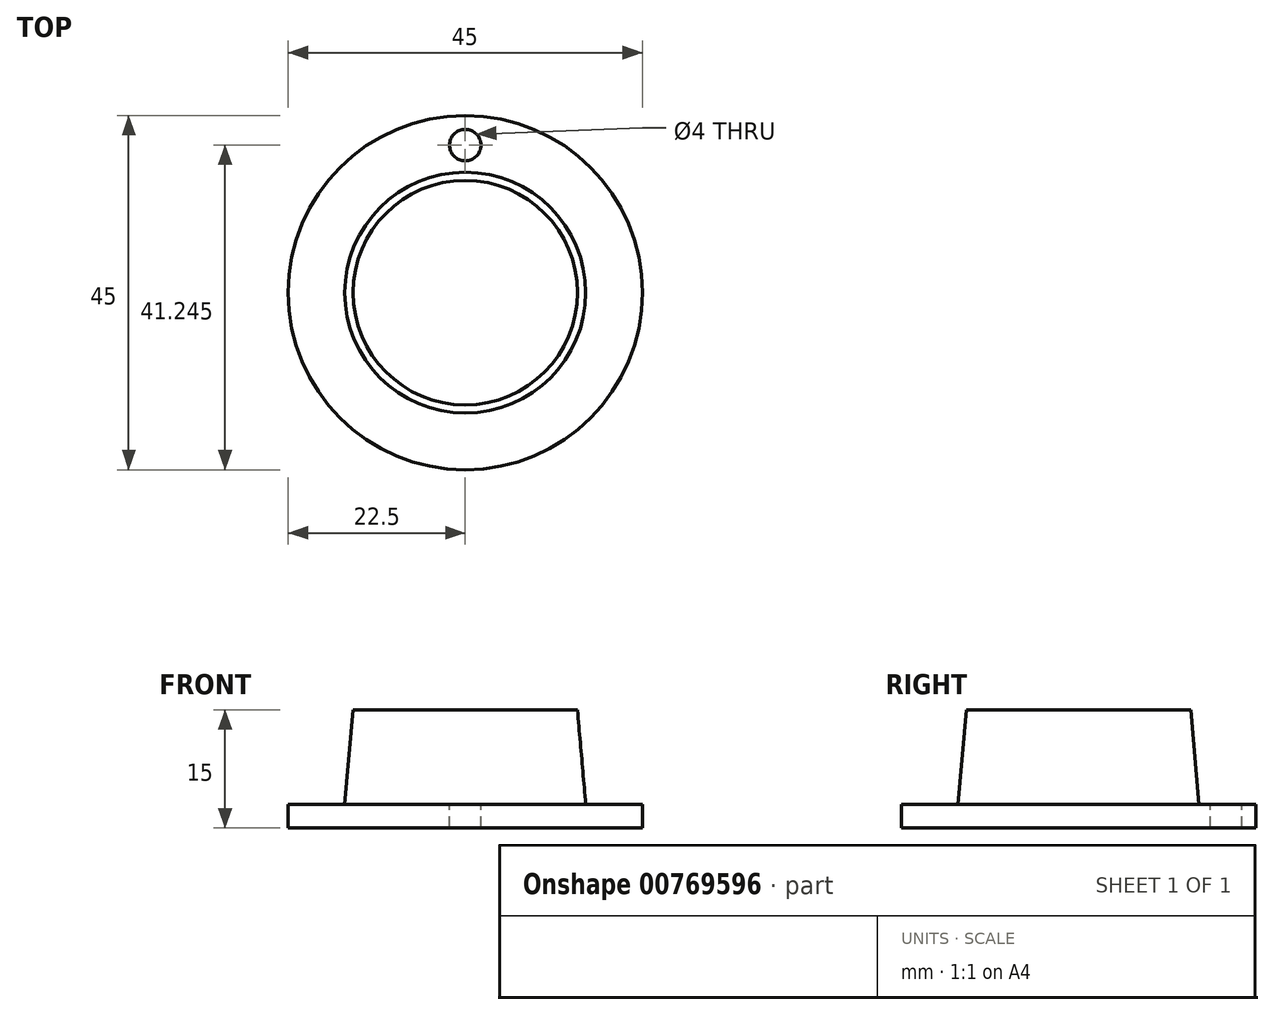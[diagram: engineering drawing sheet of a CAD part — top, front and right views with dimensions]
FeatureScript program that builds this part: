
annotation { "Feature Type Name" : "Feature", "Feature Type Description" : "" }
export const myFeature = defineFeature(function(context is Context, id is Id, definition is map)
    precondition{}
    {
        {
            var Q0;
            Q0=qCreatedBy(makeId("Top.planeOp"),FACE);
            var sketch = newSketch(context, id + "F0", { "sketchPlane" : qUnion([Q0])});
            skCircle(sketch, "E0", {"center": v(0, 0) * mm, "radius": 22.5 * mm});
            skCircle(sketch, "E1", {"center": v(0, 0) * mm, "radius": 15.3 * mm});
            skSolve(sketch);
        }
        {
            var Q0;
            Q0=makeQuery(id+"F0.imprint","IMPRINT",FACE,{"disambiguationData":[TD([[makeQuery(id+"F0.imprint","IMPRINT",EDGE,{"derivedFrom":sQuery(id+"F0.wireOp",EDGE,"E0")}),1.0]])]});
            var Q1;
            Q1=makeQuery(id+"F0.imprint","IMPRINT",FACE,{"disambiguationData":[TD([[makeQuery(id+"F0.imprint","IMPRINT",EDGE,{"derivedFrom":sQuery(id+"F0.wireOp",EDGE,"E1")}),1.0]])]});
            extrude(context, id + "F1", {"entities" : qUnion([Q0, Q1]), "depth" : 3 * mm, "offsetDistance" : 25 * mm});
        }
        {
            var Q0;
            Q0=makeQuery(id+"F1.opExtrude","CAP_FACE",FACE,{"disambiguationData":[OSD([sQuery(id+"F0.wireOp",EDGE,"E0")])],"isStart":false});
            var sketch = newSketch(context, id + "F2", { "sketchPlane" : qUnion([Q0])});
            skCircle(sketch, "E2", {"center": v(0, 0) * mm, "radius": 15.3 * mm});
            skSolve(sketch);
        }
        {
            var Q0;
            Q0=makeQuery(id+"F2.imprint","IMPRINT",FACE,{"disambiguationData":[TD([[makeQuery(id+"F2.imprint","IMPRINT",EDGE,{"derivedFrom":sQuery(id+"F2.wireOp",EDGE,"E2")}),1.0]])]});
            extrude(context, id + "F3", {"entities" : qUnion([Q0]), "operationType" : NewBodyOperationType.ADD, "depth" : 12 * mm, "offsetDistance" : 25 * mm, "hasDraft" : true, "draftAngle" : 5 * degree, "draftPullDirection" : true});
        }
        {
            var Q0;
            Q0=makeQuery(id+"F1.opExtrude","CAP_FACE",FACE,{"disambiguationData":[OSD([sQuery(id+"F0.wireOp",EDGE,"E0")])],"isStart":false});
            var sketch = newSketch(context, id + "F4", { "sketchPlane" : qUnion([Q0])});
            skCircle(sketch, "E3", {"center": v(0, 18.74) * mm, "radius": 2 * mm});
            skSolve(sketch);
        }
        {
            var Q0;
            Q0=makeQuery(id+"F4.imprint","IMPRINT",FACE,{"disambiguationData":[TD([[makeQuery(id+"F4.imprint","IMPRINT",EDGE,{"derivedFrom":sQuery(id+"F4.wireOp",EDGE,"E3")}),1.0]])]});
            extrude(context, id + "F5", {"entities" : qUnion([Q0]), "operationType" : NewBodyOperationType.REMOVE, "oppositeDirection" : true, "depth" : 32.3 * mm, "offsetDistance" : 25 * mm});
        }
    });
